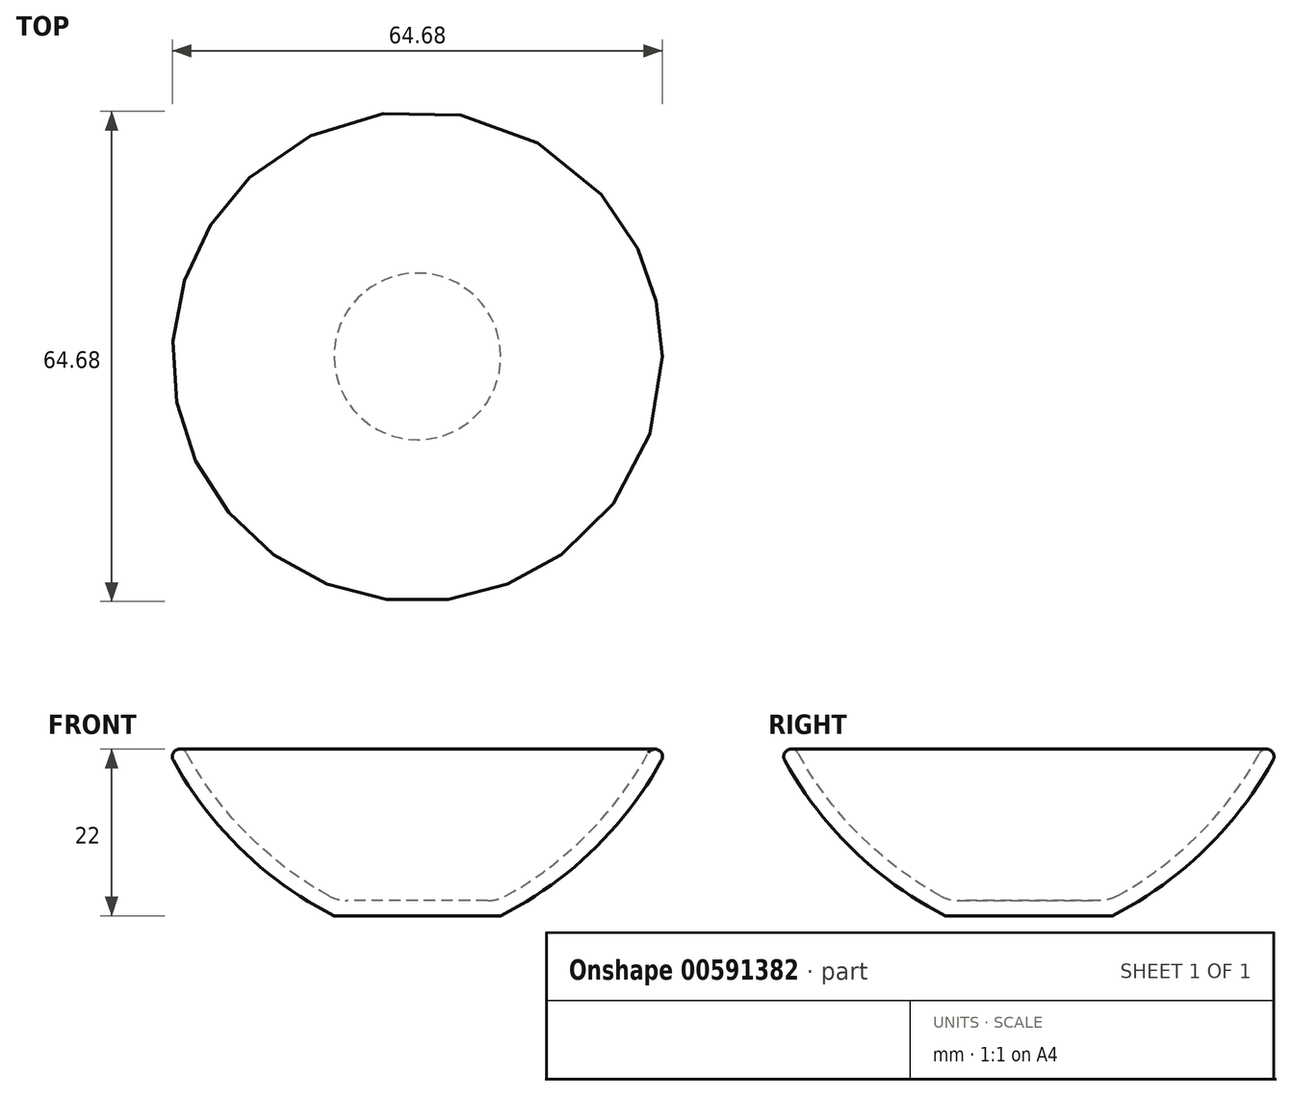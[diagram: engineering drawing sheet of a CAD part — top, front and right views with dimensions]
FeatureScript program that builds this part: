
annotation { "Feature Type Name" : "Feature", "Feature Type Description" : "" }
export const myFeature = defineFeature(function(context is Context, id is Id, definition is map)
    precondition{}
    {
        {
            var Q0;
            Q0=qCreatedBy(makeId("Front.planeOp"),FACE);
            var sketch = newSketch(context, id + "F0", { "sketchPlane" : qUnion([Q0])});
            skLineSegment(sketch, "E0", {"start": v(0, -32.17) * mm, "end": v(0, 33.92) * mm, "construction": true});
            skArc(sketch, "E1", {"start": v(11, 0) * mm, "mid": v(23.75, 9.25) * mm, "end": v(33, 22) * mm});
            skLineSegment(sketch, "E2", {"start": v(11, 0) * mm, "end": v(0, 0) * mm});
            skLineSegment(sketch, "E3", {"start": v(33, 22) * mm, "end": v(0, 22) * mm});
            skLineSegment(sketch, "E4", {"start": v(0, 22) * mm, "end": v(0, 0) * mm});
            skSolve(sketch);
        }
        {
            var Q0;
            Q0=makeQuery(id+"F0.imprint","IMPRINT",FACE,{"disambiguationData":[TD([[makeQuery(id+"F0.imprint","IMPRINT",EDGE,{"derivedFrom":sQuery(id+"F0.wireOp",EDGE,"E1")}),1.0]])]});
            var Q1;
            Q1=sQuery(id+"F0.wireOp",EDGE,"E0");
            revolve(context, id + "F1", {"entities" : qUnion([Q0]), "axis" : qUnion([Q1]), "revolveType" : RevolveType.FULL});
        }
        {
            var Q0;
            Q0=makeQuery(id+"F1.opRevolve","SWEPT_FACE",FACE,{"disambiguationData":[OSD([sQuery(id+"F0.wireOp",EDGE,"E3")])]});
            shell(context, id + "F2", {"entities" : qUnion([Q0]), "thickness" : 2 * mm});
        }
        {
            var Q0;
            Q0=makeQuery(id+"F1.opRevolve","SWEPT_EDGE",EDGE,{"disambiguationData":[OSD([sQuery(id+"F0.wireOp",EDGE,"E1"),sQuery(id+"F0.wireOp",EDGE,"E3")])]});
            var Q1;
            Q1=makeQuery(id+"F2.opShell","OFFSET_EDGE",EDGE,{"disambiguationData":[OSD([sQuery(id+"F0.wireOp",EDGE,"E1"),sQuery(id+"F0.wireOp",EDGE,"E3")])]});
            fillet(context, id + "F3", {"entities" : qUnion([Q0, Q1]), "radius" : 1 * mm, "tangentPropagation" : true, "allowEdgeOverflow" : false});
        }
        {
            var Q0;
            Q0=makeQuery(id+"F2.opShell","OFFSET_EDGE",EDGE,{"disambiguationData":[OSD([sQuery(id+"F0.wireOp",EDGE,"E1"),sQuery(id+"F0.wireOp",EDGE,"E2")])]});
            fillet(context, id + "F4", {"entities" : qUnion([Q0]), "radius" : 5 * mm, "tangentPropagation" : true, "allowEdgeOverflow" : false});
        }
    });
